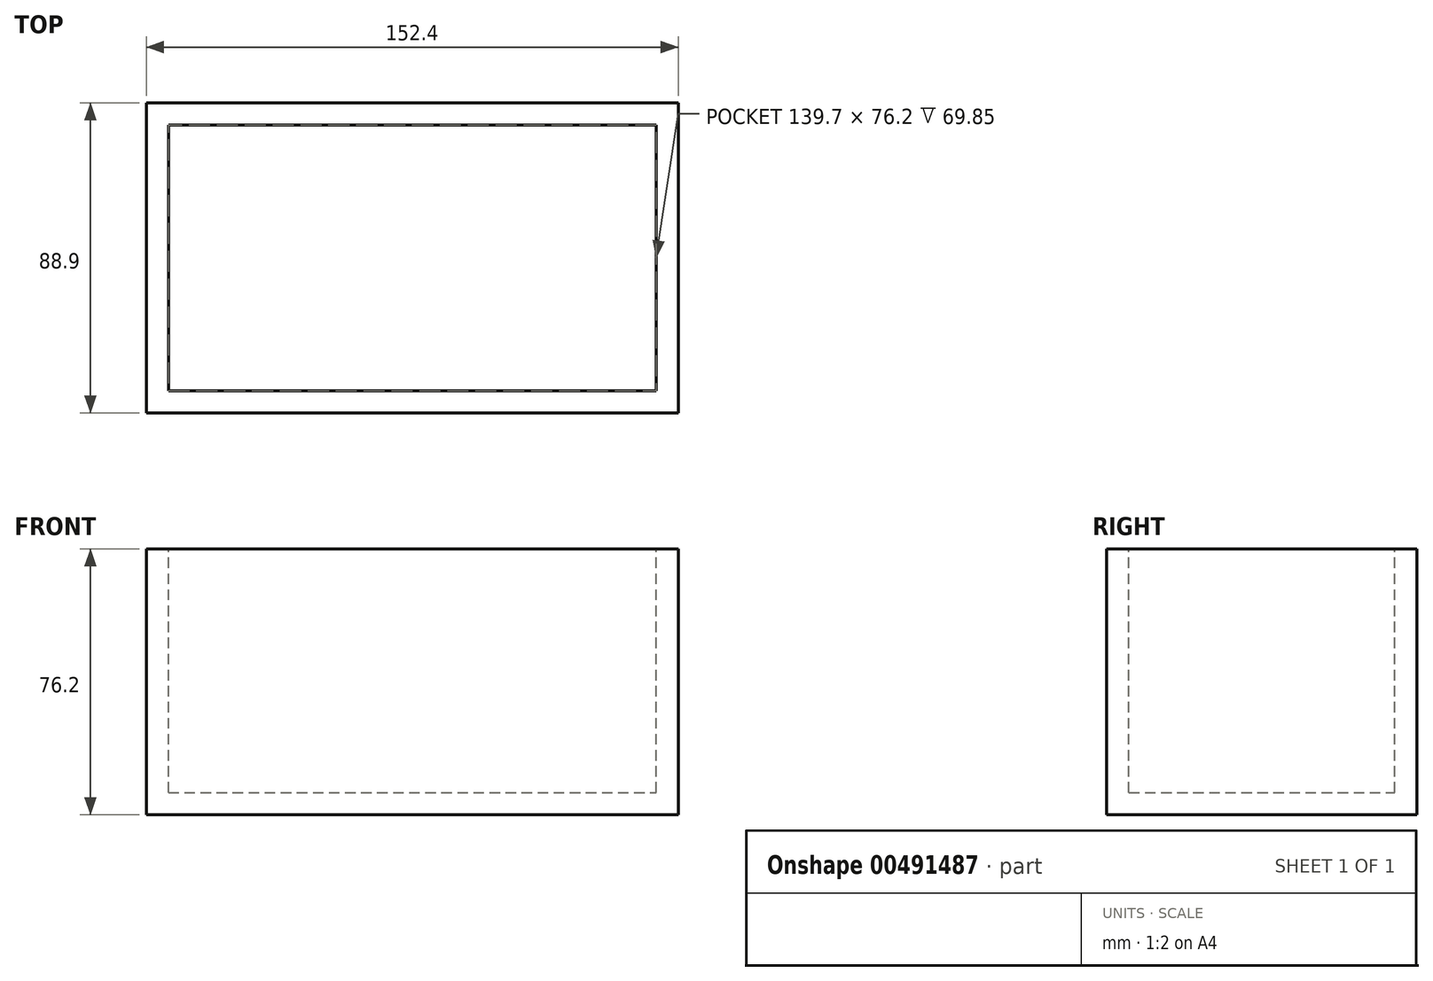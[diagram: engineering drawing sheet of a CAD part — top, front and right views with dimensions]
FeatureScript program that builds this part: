
annotation { "Feature Type Name" : "Feature", "Feature Type Description" : "" }
export const myFeature = defineFeature(function(context is Context, id is Id, definition is map)
    precondition{}
    {
        {
            var Q0;
            Q0=qCreatedBy(makeId("Top.planeOp"),FACE);
            var sketch = newSketch(context, id + "F0", { "sketchPlane" : qUnion([Q0])});
            skLineSegment(sketch, "E0.bottom", {"start": v(76.2, -44.45) * mm, "end": v(-76.2, -44.45) * mm});
            skLineSegment(sketch, "E0.top", {"start": v(76.2, 44.45) * mm, "end": v(-76.2, 44.45) * mm});
            skLineSegment(sketch, "E0.left", {"start": v(76.2, -44.45) * mm, "end": v(76.2, 44.45) * mm});
            skLineSegment(sketch, "E0.right", {"start": v(-76.2, -44.45) * mm, "end": v(-76.2, 44.45) * mm});
            skPoint(sketch, "E0.middle", {"position": v(0, 0) * mm});
            skLineSegment(sketch, "E1", {"start": v(0, 44.45) * mm, "end": v(0, 38.1) * mm});
            skPoint(sketch, "E1.endSnap0", {"position": v(0, 44.45) * mm});
            skLineSegment(sketch, "E2", {"start": v(0, -44.45) * mm, "end": v(0, -38.1) * mm});
            skPoint(sketch, "E3", {"position": v(-69.85, -38.1) * mm});
            skPoint(sketch, "E4", {"position": v(-69.85, 38.1) * mm});
            skPoint(sketch, "E5", {"position": v(69.85, 38.1) * mm});
            skLineSegment(sketch, "E6.bottom", {"start": v(-69.85, -38.1) * mm, "end": v(69.85, -38.1) * mm});
            skLineSegment(sketch, "E6.top", {"start": v(-69.85, 38.1) * mm, "end": v(69.85, 38.1) * mm});
            skLineSegment(sketch, "E6.left", {"start": v(-69.85, -38.1) * mm, "end": v(-69.85, 38.1) * mm});
            skLineSegment(sketch, "E6.right", {"start": v(69.85, -38.1) * mm, "end": v(69.85, 38.1) * mm});
            skSolve(sketch);
        }
        {
            var Q0;
            {var subQ3=sQuery(id+"F0.wireOp",EDGE,"E6.left");Q0=makeQuery(id+"F0.imprint","IMPRINT",FACE,{"disambiguationData":[TD([[makeQuery(id+"F0.imprint","IMPRINT",EDGE,{"derivedFrom":subQ3}),-1.0]])]});}
            var Q1;
            {var subQ0=sQuery(id+"F0.wireOp",EDGE,"E0.right");Q1=makeQuery(id+"F0.imprint","IMPRINT",FACE,{"disambiguationData":[TD([[makeQuery(id+"F0.imprint","IMPRINT",EDGE,{"derivedFrom":subQ0}),-1.0]])]});}
            var Q2;
            {var subQ1=sQuery(id+"F0.wireOp",EDGE,"E0.left");Q2=makeQuery(id+"F0.imprint","IMPRINT",FACE,{"disambiguationData":[TD([[makeQuery(id+"F0.imprint","IMPRINT",EDGE,{"derivedFrom":subQ1}),1.0]])]});}
            extrude(context, id + "F1", {"entities" : qUnion([Q0, Q1, Q2]), "oppositeDirection" : true, "depth" : 76.2 * mm});
        }
        {
            var Q0;
            {var subQ3=sQuery(id+"F0.wireOp",EDGE,"E6.left");Q0=makeQuery(id+"F0.imprint","IMPRINT",FACE,{"disambiguationData":[TD([[makeQuery(id+"F0.imprint","IMPRINT",EDGE,{"derivedFrom":subQ3}),-1.0]])]});}
            extrude(context, id + "F2", {"entities" : qUnion([Q0]), "operationType" : NewBodyOperationType.REMOVE, "oppositeDirection" : true, "depth" : 69.85 * mm});
        }
    });
